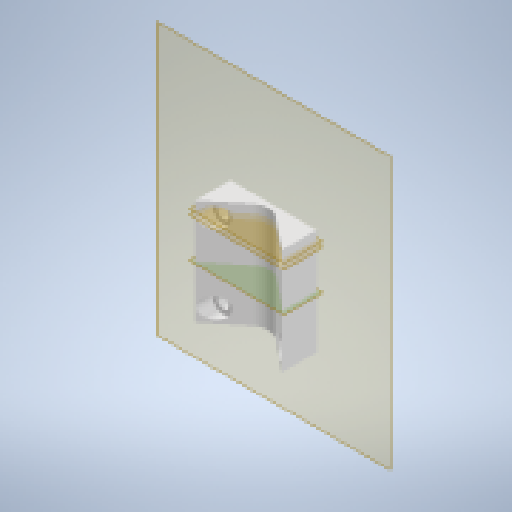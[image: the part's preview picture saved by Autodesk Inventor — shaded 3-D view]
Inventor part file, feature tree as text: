
AUTODESK INVENTOR PART (.ipt)
format: ipt  version: 2024.2 (Build 282272000, 272)  size: 219,648 bytes
history: native  units: mm
features: other x10, sketch x5, extrude x3, mirror x3, revolve x2, reference x1, projected_geometry x1
ambient origin geometry x8: Origin, YZ Plane, XZ Plane, XY Plane, X Axis, Y Axis, Z Axis, Center Point
bodies: Body1 (feature_tree)
feature tree (25):
  other  "Твердое тело1"
  other  "РабПлоскость1"
  extrude  "Выдавливание1"  Depth=3.0mm
  extrude  "Выдавливание2"  Depth=3.0mm
  other  "Сопряжение грани1"
  other  "РабПлоскость3"
  revolve  "Вращение1"
  revolve  "Вращение2"
  other  "РабПлоскость4"
  mirror  "Зеркальное отражение1"
  extrude  "Выдавливание3"  Depth=4.0mm
  other  "РабПлоскость5"
  mirror  "Зеркальное отражение2"
  mirror  "Зеркальное отражение3"
  sketch  "Эскиз1"
  reference  "Ссылка1"
  sketch  "Эскиз2"
  other  "РабПлоскость2"
  sketch  "Эскиз3"
  sketch  "Эскиз4"
  projected_geometry  "Спроецированная петля1"
  sketch  "Эскиз5"
  other  "<userpath>\Documents\Artist\3D\каретка.iam"
  other  "каретка.iam"
  other  "ANY:5"
